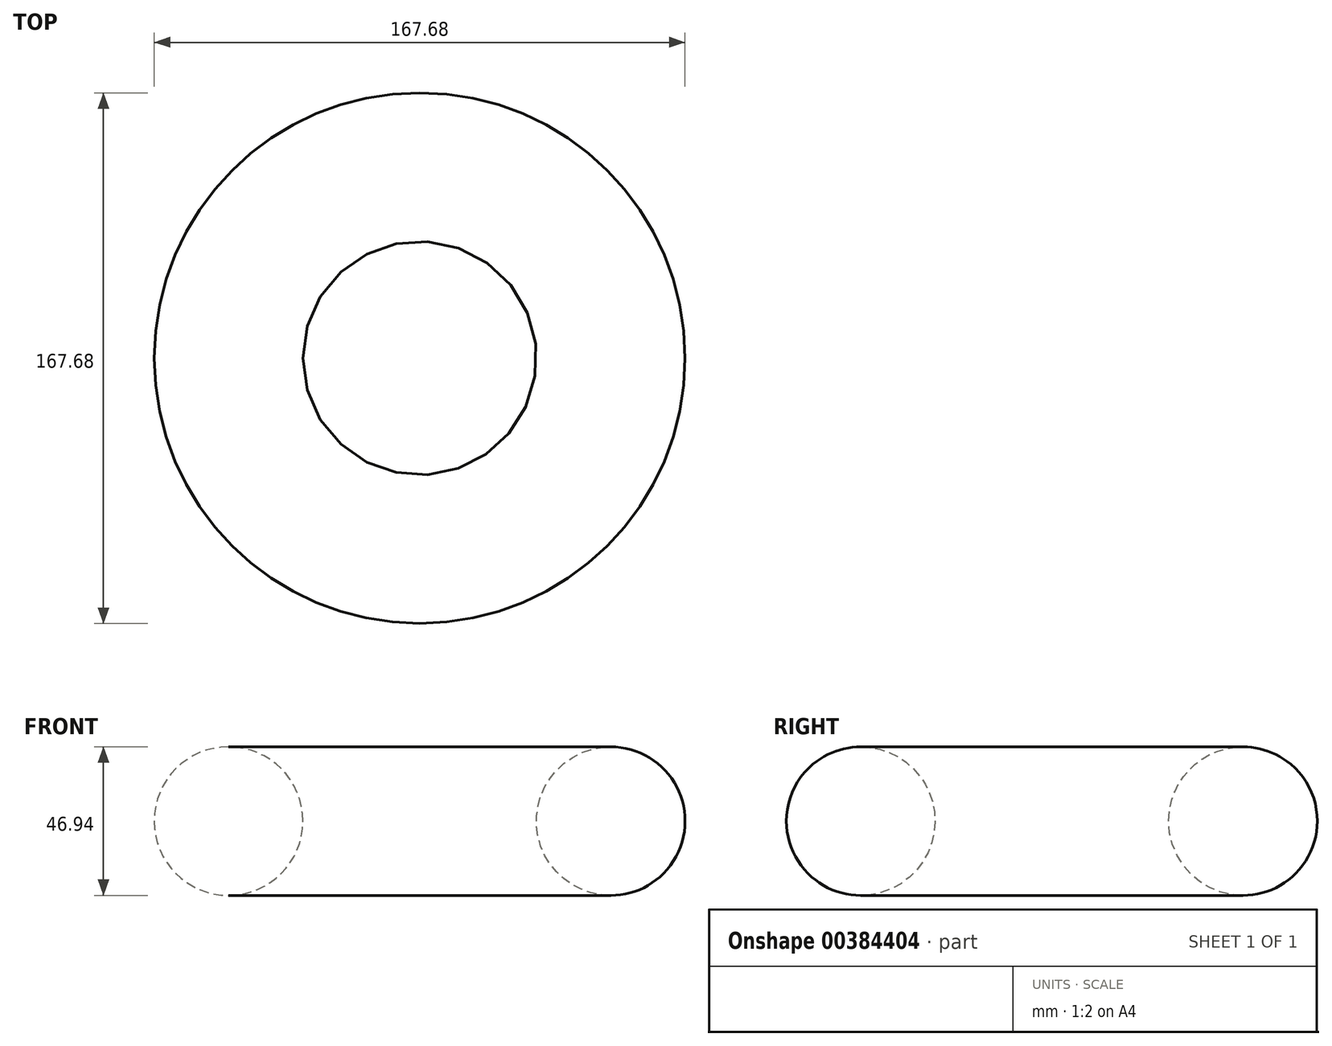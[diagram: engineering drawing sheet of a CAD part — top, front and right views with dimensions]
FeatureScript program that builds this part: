
annotation { "Feature Type Name" : "Feature", "Feature Type Description" : "" }
export const myFeature = defineFeature(function(context is Context, id is Id, definition is map)
    precondition{}
    {
        {
            var Q0;
            Q0=qCreatedBy(makeId("Front.planeOp"),FACE);
            var sketch = newSketch(context, id + "F0", { "sketchPlane" : qUnion([Q0])});
            skCircle(sketch, "E0", {"center": v(60.36, 0) * mm, "radius": 23.47 * mm});
            skLineSegment(sketch, "E1", {"start": v(0, 0) * mm, "end": v(0, 101.45) * mm});
            skSolve(sketch);
        }
        {
            var Q0;
            Q0=makeQuery(id+"F0.imprint","IMPRINT",FACE,{"disambiguationData":[TD([[makeQuery(id+"F0.imprint","IMPRINT",EDGE,{"derivedFrom":sQuery(id+"F0.wireOp",EDGE,"E0")}),1.0]])]});
            var Q1;
            Q1=sQuery(id+"F0.wireOp",EDGE,"E1");
            revolve(context, id + "F1", {"entities" : qUnion([Q0]), "axis" : qUnion([Q1]), "revolveType" : RevolveType.FULL});
        }
    });
